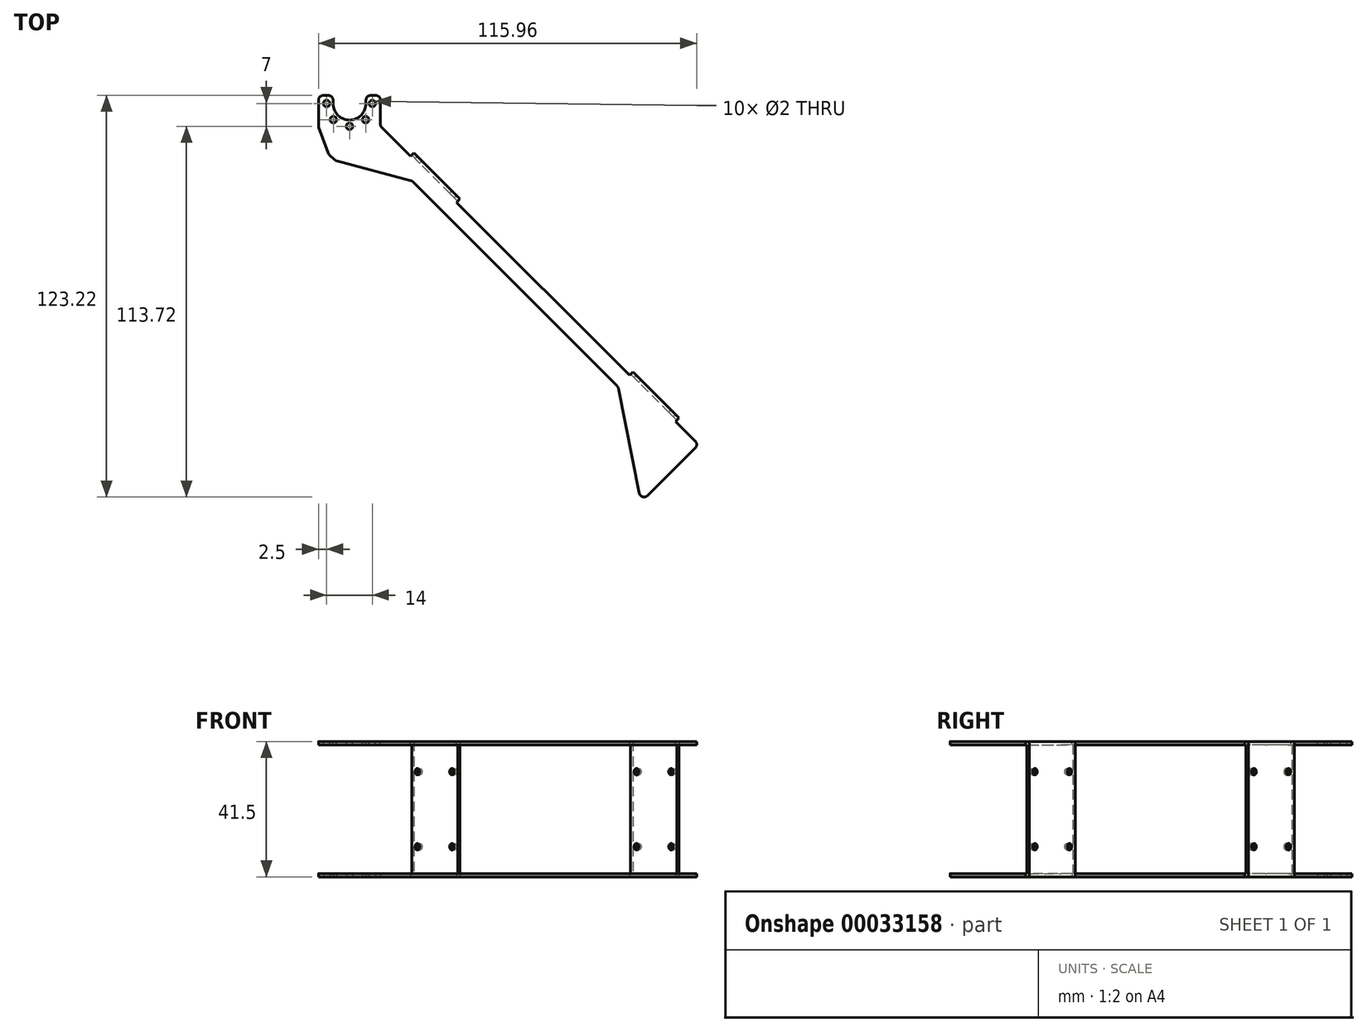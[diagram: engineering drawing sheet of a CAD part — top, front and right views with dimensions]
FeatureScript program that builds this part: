
annotation { "Feature Type Name" : "Feature", "Feature Type Description" : "" }
export const myFeature = defineFeature(function(context is Context, id is Id, definition is map)
    precondition{}
    {
        {
            var Q0;
            Q0=qCreatedBy(makeId("Top.planeOp"),FACE);
            var sketch = newSketch(context, id + "F0", { "sketchPlane" : qUnion([Q0])});
            skArc(sketch, "E0", {"start": v(-5.05, 0) * mm, "mid": v(0, -5.05) * mm, "end": v(5.05, 0) * mm});
            skCircle(sketch, "E1", {"center": v(-7, 0) * mm, "radius": 1 * mm});
            skCircle(sketch, "E2.1.0", {"center": v(-4.95, -4.95) * mm, "radius": 1 * mm});
            skCircle(sketch, "E2.2.0", {"center": v(0, -7) * mm, "radius": 1 * mm});
            skCircle(sketch, "E2.3.0", {"center": v(4.95, -4.95) * mm, "radius": 1 * mm});
            skCircle(sketch, "E2.4.0", {"center": v(7, 0) * mm, "radius": 1 * mm});
            skLineSegment(sketch, "E3", {"start": v(0, 0) * mm, "end": v(106.07, -106.07) * mm, "construction": true});
            skLineSegment(sketch, "E4", {"start": v(9.5, 0) * mm, "end": v(9.5, -7) * mm});
            skLineSegment(sketch, "E5", {"start": v(9.5, -7) * mm, "end": v(107.08, -104.58) * mm});
            skLineSegment(sketch, "E6.MirrorCS", {"start": v(-9.5, 0) * mm, "end": v(-9.5, -7) * mm});
            skLineSegment(sketch, "E7", {"start": v(-9.5, -7) * mm, "end": v(-5.85, -17.02) * mm});
            skLineSegment(sketch, "E8", {"start": v(-5.85, -17.02) * mm, "end": v(19.15, -23.72) * mm});
            skLineSegment(sketch, "E9", {"start": v(19.15, -23.72) * mm, "end": v(103.55, -108.12) * mm});
            skLineSegment(sketch, "E10", {"start": v(107.08, -104.58) * mm, "end": v(103.55, -108.12) * mm});
            skLineSegment(sketch, "E11", {"start": v(-9.5, 0) * mm, "end": v(-9.5, 2.5) * mm});
            skLineSegment(sketch, "E12", {"start": v(-9.5, 2.5) * mm, "end": v(-5.05, 2.5) * mm});
            skLineSegment(sketch, "E13", {"start": v(9.5, 2.5) * mm, "end": v(9.5, 0) * mm});
            skLineSegment(sketch, "E14", {"start": v(-5.05, 0) * mm, "end": v(-5.05, 2.5) * mm});
            skLineSegment(sketch, "E15.MirrorCS", {"start": v(5.05, 0) * mm, "end": v(5.05, 2.5) * mm});
            skLineSegment(sketch, "E16.trimOffspring", {"start": v(5.05, 2.5) * mm, "end": v(9.5, 2.5) * mm});
            skLineSegment(sketch, "E17", {"start": v(103.55, -108.12) * mm, "end": v(89.4, -122.26) * mm});
            skLineSegment(sketch, "E18", {"start": v(89.4, -122.26) * mm, "end": v(82.33, -86.9) * mm});
            skSolve(sketch);
        }
        {
            var Q0;
            Q0 = qSketchRegion(id + "F0", true);
            extrude(context, id + "F1", {"entities" : qUnion([Q0]), "depth" : 1 * mm});
        }
        {
            var Q0;
            Q0=makeQuery(id+"F1.opExtrude","SWEPT_EDGE",EDGE,{"disambiguationData":[OSD([sQuery(id+"F0.wireOp",EDGE,"E17"),sQuery(id+"F0.wireOp",EDGE,"E18")])]});
            var Q1;
            Q1=makeQuery(id+"F1.opExtrude","SWEPT_EDGE",EDGE,{"disambiguationData":[OSD([sQuery(id+"F0.wireOp",EDGE,"E9"),sQuery(id+"F0.wireOp",EDGE,"E18")])]});
            var Q2;
            Q2=makeQuery(id+"F1.opExtrude","SWEPT_EDGE",EDGE,{"disambiguationData":[OSD([sQuery(id+"F0.wireOp",EDGE,"E5"),sQuery(id+"F0.wireOp",EDGE,"E10")])]});
            var Q3;
            Q3=makeQuery(id+"F1.opExtrude","SWEPT_EDGE",EDGE,{"disambiguationData":[OSD([sQuery(id+"F0.wireOp",EDGE,"E8"),sQuery(id+"F0.wireOp",EDGE,"E9")])]});
            var Q4;
            Q4=makeQuery(id+"F1.opExtrude","SWEPT_EDGE",EDGE,{"disambiguationData":[OSD([sQuery(id+"F0.wireOp",EDGE,"E4"),sQuery(id+"F0.wireOp",EDGE,"E5")])]});
            var Q5;
            Q5=makeQuery(id+"F1.opExtrude","SWEPT_EDGE",EDGE,{"disambiguationData":[OSD([sQuery(id+"F0.wireOp",EDGE,"E13"),sQuery(id+"F0.wireOp",EDGE,"E16.trimOffspring")])]});
            var Q6;
            Q6=makeQuery(id+"F1.opExtrude","SWEPT_EDGE",EDGE,{"disambiguationData":[OSD([sQuery(id+"F0.wireOp",EDGE,"E12"),sQuery(id+"F0.wireOp",EDGE,"E14")])]});
            var Q7;
            Q7=makeQuery(id+"F1.opExtrude","SWEPT_EDGE",EDGE,{"disambiguationData":[OSD([sQuery(id+"F0.wireOp",EDGE,"E15.MirrorCS"),sQuery(id+"F0.wireOp",EDGE,"E16.trimOffspring")])]});
            var Q8;
            Q8=makeQuery(id+"F1.opExtrude","SWEPT_EDGE",EDGE,{"disambiguationData":[OSD([sQuery(id+"F0.wireOp",EDGE,"E11"),sQuery(id+"F0.wireOp",EDGE,"E12")])]});
            var Q9;
            Q9=makeQuery(id+"F1.opExtrude","SWEPT_EDGE",EDGE,{"disambiguationData":[OSD([sQuery(id+"F0.wireOp",EDGE,"E6.MirrorCS"),sQuery(id+"F0.wireOp",EDGE,"E7")])]});
            fillet(context, id + "F2", {"entities" : qUnion([Q0, Q1, Q2, Q3, Q4, Q5, Q6, Q7, Q8, Q9]), "radius" : 1.5 * mm, "tangentPropagation" : true, "allowEdgeOverflow" : false});
        }
        {
            var Q0;
            Q0=makeQuery(id+"F1.opExtrude","SWEPT_EDGE",EDGE,{"disambiguationData":[OSD([sQuery(id+"F0.wireOp",EDGE,"E7"),sQuery(id+"F0.wireOp",EDGE,"E8")])]});
            chamfer(context, id + "F3", {"entities" : qUnion([Q0]), "width" : 3 * mm, "tangentPropagation" : true});
        }
        {
            var Q0;
            {var subQ0=sQuery(id+"F0.wireOp",EDGE,"E7");Q0=makeQuery(id+"F3.opChamfer","BLEND_EDGE",EDGE,{"blendedFrom":[makeQuery(id+"F1.opExtrude","SWEPT_EDGE",EDGE,{"disambiguationData":[OSD([subQ0,sQuery(id+"F0.wireOp",EDGE,"E8")])]}),makeQuery(id+"F1.opExtrude","SWEPT_FACE",FACE,{"disambiguationData":[OSD([subQ0])]})],"blendedInto":[makeQuery(id+"F1.opExtrude","SWEPT_FACE",FACE,{"disambiguationData":[OSD([subQ0])]})]});}
            var Q1;
            {var subQ0=sQuery(id+"F0.wireOp",EDGE,"E8");Q1=makeQuery(id+"F3.opChamfer","BLEND_EDGE",EDGE,{"blendedFrom":[makeQuery(id+"F1.opExtrude","SWEPT_EDGE",EDGE,{"disambiguationData":[OSD([sQuery(id+"F0.wireOp",EDGE,"E7"),subQ0])]}),makeQuery(id+"F1.opExtrude","SWEPT_FACE",FACE,{"disambiguationData":[OSD([subQ0])]})],"blendedInto":[makeQuery(id+"F1.opExtrude","SWEPT_FACE",FACE,{"disambiguationData":[OSD([subQ0])]})]});}
            fillet(context, id + "F4", {"entities" : qUnion([Q0, Q1]), "radius" : 1.5 * mm, "tangentPropagation" : true, "allowEdgeOverflow" : false});
        }
        {
            var Q0;
            Q0=makeQuery(id+"F1.opExtrude","CAP_FACE",FACE,{"disambiguationData":[OSD([sQuery(id+"F0.wireOp",EDGE,"E0"),sQuery(id+"F0.wireOp",EDGE,"E1"),sQuery(id+"F0.wireOp",EDGE,"E2.1.0"),sQuery(id+"F0.wireOp",EDGE,"E2.2.0"),sQuery(id+"F0.wireOp",EDGE,"E2.3.0"),sQuery(id+"F0.wireOp",EDGE,"E2.4.0"),sQuery(id+"F0.wireOp",EDGE,"E4"),sQuery(id+"F0.wireOp",EDGE,"E5"),sQuery(id+"F0.wireOp",EDGE,"E6.MirrorCS"),sQuery(id+"F0.wireOp",EDGE,"E7"),sQuery(id+"F0.wireOp",EDGE,"E8"),sQuery(id+"F0.wireOp",EDGE,"E9"),sQuery(id+"F0.wireOp",EDGE,"E10"),sQuery(id+"F0.wireOp",EDGE,"E11"),sQuery(id+"F0.wireOp",EDGE,"E12"),sQuery(id+"F0.wireOp",EDGE,"E13"),sQuery(id+"F0.wireOp",EDGE,"E14"),sQuery(id+"F0.wireOp",EDGE,"E15.MirrorCS"),sQuery(id+"F0.wireOp",EDGE,"E16.trimOffspring"),sQuery(id+"F0.wireOp",EDGE,"E17"),sQuery(id+"F0.wireOp",EDGE,"E18")])],"isStart":false});
            var sketch = newSketch(context, id + "F5", { "sketchPlane" : qUnion([Q0])});
            skLineSegment(sketch, "E19", {"start": v(18.7, -16.2) * mm, "end": v(19.75, -15.13) * mm});
            skLineSegment(sketch, "E20", {"start": v(19.75, -15.13) * mm, "end": v(33.9, -29.27) * mm});
            skLineSegment(sketch, "E21", {"start": v(33.9, -29.27) * mm, "end": v(32.83, -30.33) * mm});
            skLineSegment(sketch, "E22", {"start": v(18.7, -16.2) * mm, "end": v(32.83, -30.33) * mm});
            skLineSegment(sketch, "E23", {"start": v(100, -97.5) * mm, "end": v(85.87, -83.37) * mm});
            skLineSegment(sketch, "E24", {"start": v(85.87, -83.37) * mm, "end": v(86.93, -82.3) * mm});
            skLineSegment(sketch, "E25", {"start": v(86.93, -82.3) * mm, "end": v(101.07, -96.45) * mm});
            skLineSegment(sketch, "E26", {"start": v(101.07, -96.45) * mm, "end": v(100, -97.5) * mm});
            skSolve(sketch);
        }
        {
            var Q0;
            Q0 = qSketchRegion(id + "F5", true);
            extrude(context, id + "F6", {"entities" : qUnion([Q0]), "operationType" : NewBodyOperationType.ADD, "depth" : (39.5 / 2) * mm, "hasSecondDirection" : true, "secondDirectionOppositeDirection" : true, "secondDirectionDepth" : 1 * mm});
        }
        {
            var Q0;
            Q0=makeQuery(id+"F6.opExtrude","CAP_FACE",FACE,{"disambiguationData":[OSD([sQuery(id+"F5.wireOp",EDGE,"E19"),sQuery(id+"F5.wireOp",EDGE,"E20"),sQuery(id+"F5.wireOp",EDGE,"E21"),sQuery(id+"F5.wireOp",EDGE,"E22")])],"isStart":false});
            cPlane(context, id + "F7", {"entities" : qUnion([Q0]), "cplaneType" : CPlaneType.OFFSET, "offset" : 0 * mm, "width" : 150 * mm, "height" : 150 * mm});
        }
        {
            var Q0;
            Q0=makeQuery(id+"F1.opExtrude","SWEPT_BODY",BODY,{"disambiguationData":[OSD([sQuery(id+"F0.wireOp",EDGE,"E0"),sQuery(id+"F0.wireOp",EDGE,"E1"),sQuery(id+"F0.wireOp",EDGE,"E2.1.0"),sQuery(id+"F0.wireOp",EDGE,"E2.2.0"),sQuery(id+"F0.wireOp",EDGE,"E2.3.0"),sQuery(id+"F0.wireOp",EDGE,"E2.4.0"),sQuery(id+"F0.wireOp",EDGE,"E4"),sQuery(id+"F0.wireOp",EDGE,"E5"),sQuery(id+"F0.wireOp",EDGE,"E6.MirrorCS"),sQuery(id+"F0.wireOp",EDGE,"E7"),sQuery(id+"F0.wireOp",EDGE,"E8"),sQuery(id+"F0.wireOp",EDGE,"E9"),sQuery(id+"F0.wireOp",EDGE,"E10"),sQuery(id+"F0.wireOp",EDGE,"E11"),sQuery(id+"F0.wireOp",EDGE,"E12"),sQuery(id+"F0.wireOp",EDGE,"E13"),sQuery(id+"F0.wireOp",EDGE,"E14"),sQuery(id+"F0.wireOp",EDGE,"E15.MirrorCS"),sQuery(id+"F0.wireOp",EDGE,"E16.trimOffspring"),sQuery(id+"F0.wireOp",EDGE,"E17"),sQuery(id+"F0.wireOp",EDGE,"E18")])]});
            var Q1;
            Q1=qCreatedBy(id+"F7.planeOp",FACE);
            mirror(context, id + "F8", {"operationType" : NewBodyOperationType.ADD, "entities" : qUnion([Q0]), "mirrorPlane" : qUnion([Q1])});
        }
        {
            var Q0;
            {var subQ0=makeQuery(id+"F6.opExtrude","SWEPT_FACE",FACE,{"disambiguationData":[OSD([sQuery(id+"F5.wireOp",EDGE,"E20")])]});Q0=makeQuery(id+"F8.boolean.opBoolean","MERGE",FACE,{"derivedFrom":[subQ0,makeQuery(id+"F8.opPattern","COPY",FACE,{"derivedFrom":subQ0,"instanceName":"1"})]});}
            var sketch = newSketch(context, id + "F9", { "sketchPlane" : qUnion([Q0])});
            skLineSegment(sketch, "E27", {"start": v(-24.67, 20.75) * mm, "end": v(-44.67, 20.75) * mm, "construction": true});
            skLineSegment(sketch, "E28.bottom", {"start": v(-27.17, 32.25) * mm, "end": v(-42.17, 32.25) * mm, "construction": true});
            skLineSegment(sketch, "E28.top", {"start": v(-27.17, 9.25) * mm, "end": v(-42.17, 9.25) * mm, "construction": true});
            skLineSegment(sketch, "E28.left", {"start": v(-27.17, 32.25) * mm, "end": v(-27.17, 9.25) * mm, "construction": true});
            skLineSegment(sketch, "E28.right", {"start": v(-42.17, 32.25) * mm, "end": v(-42.17, 9.25) * mm, "construction": true});
            skPoint(sketch, "E28.middle", {"position": v(-34.67, 20.75) * mm});
            skCircle(sketch, "E29", {"center": v(-27.17, 32.25) * mm, "radius": 1 * mm});
            skLineSegment(sketch, "E30", {"start": v(-34.67, 32.25) * mm, "end": v(-34.67, 9.25) * mm, "construction": true});
            skCircle(sketch, "E31.MirrorC", {"center": v(-27.17, 9.25) * mm, "radius": 1 * mm});
            skCircle(sketch, "E32.MirrorC", {"center": v(-42.17, 32.25) * mm, "radius": 1 * mm});
            skCircle(sketch, "E33.MirrorC", {"center": v(-42.17, 9.25) * mm, "radius": 1 * mm});
            skLineSegment(sketch, "E34.1.0.0", {"start": v(-122.17, 32.25) * mm, "end": v(-137.17, 32.25) * mm, "construction": true});
            skLineSegment(sketch, "E34.1.0.1", {"start": v(-129.67, 32.25) * mm, "end": v(-129.67, 9.25) * mm, "construction": true});
            skLineSegment(sketch, "E34.1.0.2", {"start": v(-122.17, 32.25) * mm, "end": v(-122.17, 9.25) * mm, "construction": true});
            skLineSegment(sketch, "E34.1.0.3", {"start": v(-119.67, 20.75) * mm, "end": v(-139.67, 20.75) * mm, "construction": true});
            skLineSegment(sketch, "E34.1.0.4", {"start": v(-137.17, 32.25) * mm, "end": v(-137.17, 9.25) * mm, "construction": true});
            skLineSegment(sketch, "E34.1.0.5", {"start": v(-122.17, 9.25) * mm, "end": v(-137.17, 9.25) * mm, "construction": true});
            skPoint(sketch, "E34.1.0.6", {"position": v(-129.67, 20.75) * mm});
            skCircle(sketch, "E34.1.0.7", {"center": v(-137.17, 32.25) * mm, "radius": 1 * mm});
            skCircle(sketch, "E34.1.0.8", {"center": v(-137.17, 9.25) * mm, "radius": 1 * mm});
            skCircle(sketch, "E34.1.0.9", {"center": v(-122.17, 9.25) * mm, "radius": 1 * mm});
            skCircle(sketch, "E34.1.0.10", {"center": v(-122.17, 32.25) * mm, "radius": 1 * mm});
            skLineSegment(sketch, "E34.direction1", {"start": v(-42.17, 9.25) * mm, "end": v(-137.17, 9.25) * mm, "construction": true});
            skSolve(sketch);
        }
        {
            var Q0;
            Q0 = qSketchRegion(id + "F9", true);
            extrude(context, id + "F10", {"entities" : qUnion([Q0]), "operationType" : NewBodyOperationType.REMOVE, "endBound" : BoundingType.UP_TO_NEXT, "oppositeDirection" : true, "depth" : 25 * mm});
        }
        {
            var Q0;
            {var subQ0=makeQuery(id+"F6.opExtrude","SWEPT_FACE",FACE,{"disambiguationData":[OSD([sQuery(id+"F5.wireOp",EDGE,"E22")])]});Q0=makeQuery(id+"F8.boolean.opBoolean","MERGE",FACE,{"derivedFrom":[subQ0,makeQuery(id+"F8.opPattern","COPY",FACE,{"derivedFrom":subQ0,"instanceName":"1"})]});}
            var sketch = newSketch(context, id + "F11", { "sketchPlane" : qUnion([Q0])});
            skLineSegment(sketch, "E35.0.0", {"start": v(24.67, 40.5) * mm, "end": v(24.67, 1) * mm});
            skLineSegment(sketch, "E35.0.1", {"start": v(24.67, 1) * mm, "end": v(44.67, 1) * mm});
            skLineSegment(sketch, "E35.0.2", {"start": v(44.67, 1) * mm, "end": v(44.67, 40.5) * mm});
            skLineSegment(sketch, "E35.0.3", {"start": v(44.67, 40.5) * mm, "end": v(24.67, 40.5) * mm});
            skLineSegment(sketch, "E36.0.0", {"start": v(119.67, 40.5) * mm, "end": v(119.67, 1) * mm});
            skLineSegment(sketch, "E36.0.1", {"start": v(119.67, 1) * mm, "end": v(139.67, 1) * mm});
            skLineSegment(sketch, "E36.0.2", {"start": v(139.67, 1) * mm, "end": v(139.67, 40.5) * mm});
            skLineSegment(sketch, "E36.0.3", {"start": v(139.67, 40.5) * mm, "end": v(119.67, 40.5) * mm});
            skCircle(sketch, "E37.0", {"center": v(42.17, 32.25) * mm, "radius": 1 * mm});
            skCircle(sketch, "E38.0", {"center": v(27.17, 9.25) * mm, "radius": 1 * mm});
            skCircle(sketch, "E39.0", {"center": v(42.17, 9.25) * mm, "radius": 1 * mm});
            skCircle(sketch, "E40.0", {"center": v(27.17, 32.25) * mm, "radius": 1 * mm});
            skCircle(sketch, "E41.0", {"center": v(122.17, 32.25) * mm, "radius": 1 * mm});
            skCircle(sketch, "E42.0", {"center": v(137.17, 32.25) * mm, "radius": 1 * mm});
            skCircle(sketch, "E43.0", {"center": v(122.17, 9.25) * mm, "radius": 1 * mm});
            skCircle(sketch, "E44.0", {"center": v(137.17, 9.25) * mm, "radius": 1 * mm});
            skSolve(sketch);
        }
        {
            var Q0;
            Q0 = qSketchRegion(id + "F11", true);
            extrude(context, id + "F12", {"entities" : qUnion([Q0]), "operationType" : NewBodyOperationType.REMOVE, "oppositeDirection" : true, "depth" : 0.5 * mm});
        }
    });
